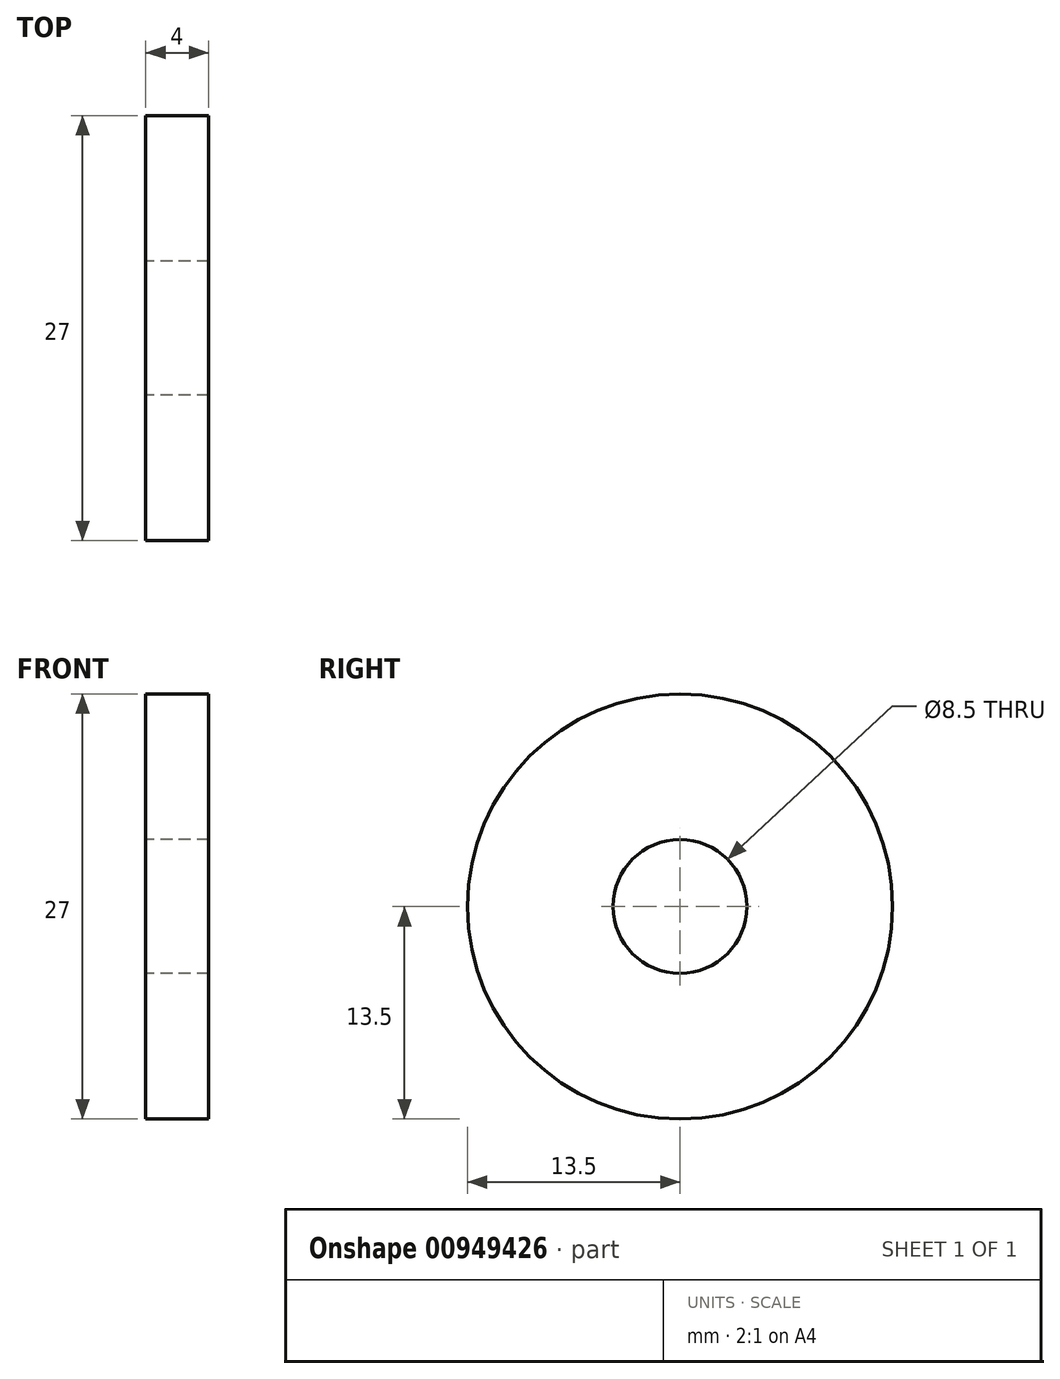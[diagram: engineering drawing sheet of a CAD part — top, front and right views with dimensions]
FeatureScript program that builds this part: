
annotation { "Feature Type Name" : "Feature", "Feature Type Description" : "" }
export const myFeature = defineFeature(function(context is Context, id is Id, definition is map)
    precondition{}
    {
        {
            var Q0;
            Q0=qCreatedBy(makeId("Right.planeOp"),FACE);
            var sketch = newSketch(context, id + "F0", { "sketchPlane" : qUnion([Q0])});
            skCircle(sketch, "E0", {"center": v(0, 0) * mm, "radius": 13.5 * mm});
            skCircle(sketch, "E1", {"center": v(0, 0) * mm, "radius": 4.25 * mm});
            skSolve(sketch);
        }
        {
            var Q0;
            Q0=makeQuery(id+"F0.imprint","IMPRINT",FACE,{"disambiguationData":[TD([[makeQuery(id+"F0.imprint","IMPRINT",EDGE,{"derivedFrom":sQuery(id+"F0.wireOp",EDGE,"E0")}),1.0]])]});
            extrude(context, id + "F1", {"entities" : qUnion([Q0]), "depth" : 4 * mm, "offsetDistance" : 25 * mm});
        }
    });
